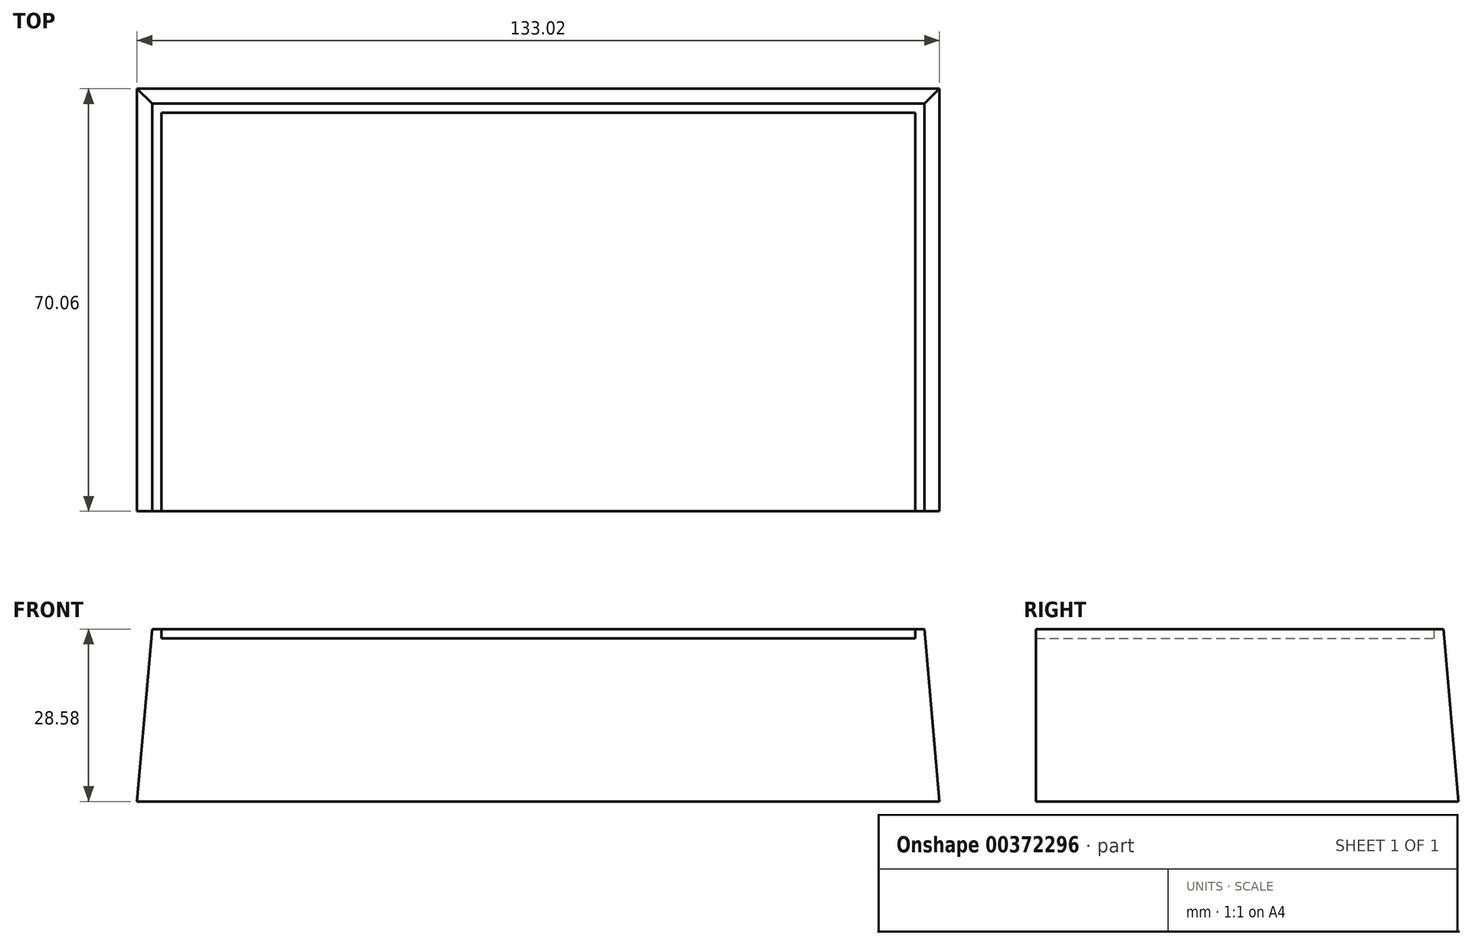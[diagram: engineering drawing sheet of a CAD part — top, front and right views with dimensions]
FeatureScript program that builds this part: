
annotation { "Feature Type Name" : "Feature", "Feature Type Description" : "" }
export const myFeature = defineFeature(function(context is Context, id is Id, definition is map)
    precondition{}
    {
        {
            var Q0;
            Q0=qCreatedBy(makeId("Top.planeOp"),FACE);
            var sketch = newSketch(context, id + "F0", { "sketchPlane" : qUnion([Q0])});
            skLineSegment(sketch, "E0.bottom", {"start": v(64, 33.78) * mm, "end": v(-64, 33.78) * mm});
            skLineSegment(sketch, "E0.top", {"start": v(64, -33.78) * mm, "end": v(-64, -33.78) * mm});
            skLineSegment(sketch, "E0.left", {"start": v(64, 33.78) * mm, "end": v(64, -33.78) * mm});
            skLineSegment(sketch, "E0.right", {"start": v(-64, 33.78) * mm, "end": v(-64, -33.78) * mm});
            skPoint(sketch, "E0.middle", {"position": v(0, 0) * mm});
            skSolve(sketch);
        }
        {
            var Q0;
            Q0=makeQuery(id+"F0.imprint","IMPRINT",FACE,{"disambiguationData":[TD([[makeQuery(id+"F0.imprint","IMPRINT",EDGE,{"derivedFrom":sQuery(id+"F0.wireOp",EDGE,"E0.bottom")}),1.0]])]});
            extrude(context, id + "F1", {"entities" : qUnion([Q0]), "oppositeDirection" : true, "depth" : 28.57 * mm, "hasDraft" : true, "draftAngle" : 5 * degree});
        }
        {
            var Q0;
            Q0=qCreatedBy(makeId("Right.planeOp"),FACE);
            var sketch = newSketch(context, id + "F2", { "sketchPlane" : qUnion([Q0])});
            skLineSegment(sketch, "E1", {"start": v(-33.78, 0) * mm, "end": v(-33.78, -28.58) * mm});
            skLineSegment(sketch, "E2", {"start": v(-33.78, -28.58) * mm, "end": v(-36.28, -28.58) * mm});
            skLineSegment(sketch, "E3", {"start": v(-36.28, -28.58) * mm, "end": v(-36.28, 0) * mm});
            skLineSegment(sketch, "E4", {"start": v(-36.28, 0) * mm, "end": v(-33.78, 0) * mm});
            skSolve(sketch);
        }
        {
            var Q0;
            Q0=makeQuery(id+"F2.imprint","IMPRINT",FACE,{"disambiguationData":[TD([[makeQuery(id+"F2.imprint","IMPRINT",EDGE,{"derivedFrom":sQuery(id+"F2.wireOp",EDGE,"E1")}),-1.0]])]});
            extrude(context, id + "F3", {"entities" : qUnion([Q0]), "operationType" : NewBodyOperationType.REMOVE, "endBound" : BoundingType.THROUGH_ALL, "oppositeDirection" : true, "depth" : 25.4 * mm, "hasSecondDirection" : true, "secondDirectionBound" : SecondDirectionBoundingType.THROUGH_ALL, "secondDirectionOppositeDirection" : false, "secondDirectionDepth" : 25.4 * mm});
        }
        {
            var Q0;
            Q0=makeQuery(id+"F1.opExtrude","CAP_FACE",FACE,{"disambiguationData":[OSD([sQuery(id+"F0.wireOp",EDGE,"E0.bottom"),sQuery(id+"F0.wireOp",EDGE,"E0.top"),sQuery(id+"F0.wireOp",EDGE,"E0.left"),sQuery(id+"F0.wireOp",EDGE,"E0.right")])],"isStart":true});
            var sketch = newSketch(context, id + "F4", { "sketchPlane" : qUnion([Q0])});
            skLineSegment(sketch, "E5", {"start": v(-62.48, -33.78) * mm, "end": v(-62.48, 32.26) * mm});
            skLineSegment(sketch, "E6", {"start": v(-62.48, 32.26) * mm, "end": v(62.48, 32.26) * mm});
            skLineSegment(sketch, "E7", {"start": v(62.48, 32.26) * mm, "end": v(62.48, -33.78) * mm});
            skLineSegment(sketch, "E8", {"start": v(62.48, -33.78) * mm, "end": v(-62.48, -33.78) * mm});
            skSolve(sketch);
        }
        {
            var Q0;
            Q0=makeQuery(id+"F4.imprint","IMPRINT",FACE,{"disambiguationData":[TD([[makeQuery(id+"F4.imprint","IMPRINT",EDGE,{"derivedFrom":sQuery(id+"F4.wireOp",EDGE,"E5")}),-1.0]])]});
            extrude(context, id + "F5", {"entities" : qUnion([Q0]), "operationType" : NewBodyOperationType.REMOVE, "oppositeDirection" : true, "depth" : 1.52 * mm});
        }
    });
